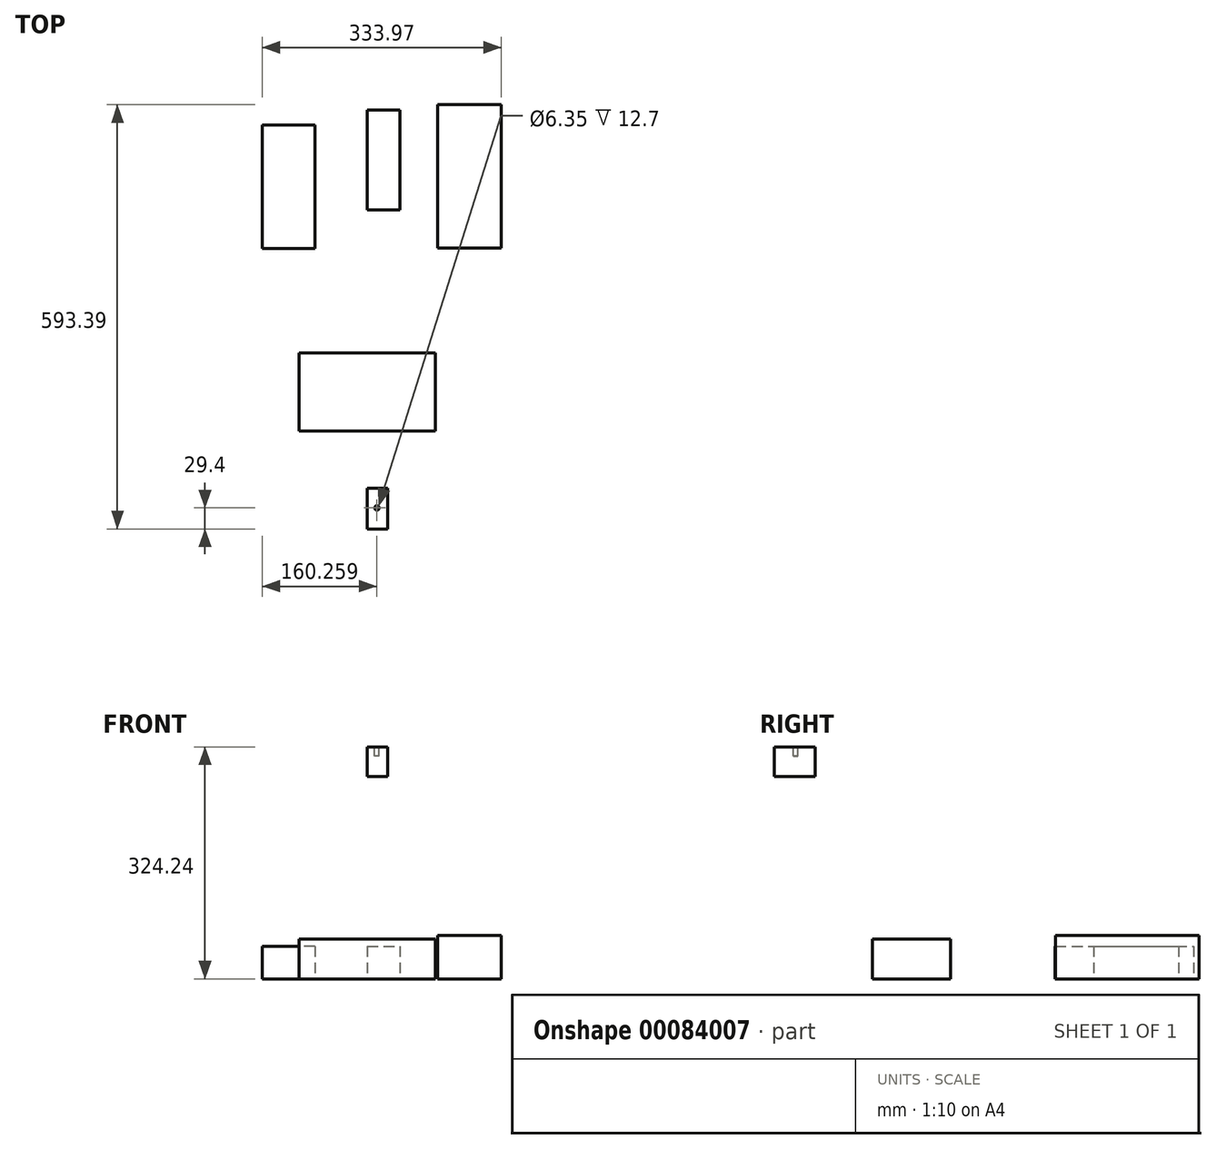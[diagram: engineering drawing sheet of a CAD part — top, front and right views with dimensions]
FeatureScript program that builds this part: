
annotation { "Feature Type Name" : "Feature", "Feature Type Description" : "" }
export const myFeature = defineFeature(function(context is Context, id is Id, definition is map)
    precondition{}
    {
        {
            var Q0;
            Q0=qCreatedBy(makeId("Top.planeOp"),FACE);
            var sketch = newSketch(context, id + "F0", { "sketchPlane" : qUnion([Q0])});
            skLineSegment(sketch, "E0.bottom", {"start": v(0, 0) * mm, "end": v(45.72, 0) * mm});
            skLineSegment(sketch, "E0.top", {"start": v(0, 139.7) * mm, "end": v(45.72, 139.7) * mm});
            skLineSegment(sketch, "E0.left", {"start": v(0, 0) * mm, "end": v(0, 139.7) * mm});
            skLineSegment(sketch, "E0.right", {"start": v(45.72, 0) * mm, "end": v(45.72, 139.7) * mm});
            skSolve(sketch);
        }
        {
            var Q0;
            Q0=makeQuery(id+"F0.imprint","IMPRINT",FACE,{"disambiguationData":[TD([[makeQuery(id+"F0.imprint","IMPRINT",EDGE,{"derivedFrom":sQuery(id+"F0.wireOp",EDGE,"E0.bottom")}),1.0]])]});
            extrude(context, id + "F1", {"entities" : qUnion([Q0]), "depth" : 45.72 * mm});
        }
        {
            var Q0;
            Q0=qCreatedBy(makeId("Top.planeOp"),FACE);
            var sketch = newSketch(context, id + "F2", { "sketchPlane" : qUnion([Q0])});
            skLineSegment(sketch, "E1.bottom", {"start": v(-72.96, -53.7) * mm, "end": v(-146.62, -53.7) * mm});
            skLineSegment(sketch, "E1.top", {"start": v(-72.96, 119.01) * mm, "end": v(-146.62, 119.01) * mm});
            skLineSegment(sketch, "E1.left", {"start": v(-72.96, -53.7) * mm, "end": v(-72.96, 119.01) * mm});
            skLineSegment(sketch, "E1.right", {"start": v(-146.62, -53.7) * mm, "end": v(-146.62, 119.01) * mm});
            skSolve(sketch);
        }
        {
            var Q0;
            Q0=makeQuery(id+"F2.imprint","IMPRINT",FACE,{"disambiguationData":[TD([[makeQuery(id+"F2.imprint","IMPRINT",EDGE,{"derivedFrom":sQuery(id+"F2.wireOp",EDGE,"E1.bottom")}),-1.0]])]});
            extrude(context, id + "F3", {"entities" : qUnion([Q0]), "depth" : 45.72 * mm});
        }
        {
            var Q0;
            Q0=qCreatedBy(makeId("Top.planeOp"),FACE);
            var sketch = newSketch(context, id + "F4", { "sketchPlane" : qUnion([Q0])});
            skLineSegment(sketch, "E2.bottom", {"start": v(98.45, -53.47) * mm, "end": v(187.35, -53.47) * mm});
            skLineSegment(sketch, "E2.top", {"start": v(98.45, 147.19) * mm, "end": v(187.35, 147.19) * mm});
            skLineSegment(sketch, "E2.left", {"start": v(98.45, -53.47) * mm, "end": v(98.45, 147.19) * mm});
            skLineSegment(sketch, "E2.right", {"start": v(187.35, -53.47) * mm, "end": v(187.35, 147.19) * mm});
            skSolve(sketch);
        }
        {
            var Q0;
            Q0=makeQuery(id+"F4.imprint","IMPRINT",FACE,{"disambiguationData":[TD([[makeQuery(id+"F4.imprint","IMPRINT",EDGE,{"derivedFrom":sQuery(id+"F4.wireOp",EDGE,"E2.bottom")}),1.0]])]});
            extrude(context, id + "F5", {"entities" : qUnion([Q0]), "depth" : 60.96 * mm});
        }
        {
            var Q0;
            Q0=qCreatedBy(makeId("Top.planeOp"),FACE);
            var sketch = newSketch(context, id + "F6", { "sketchPlane" : qUnion([Q0])});
            skLineSegment(sketch, "E3.bottom", {"start": v(-95.33, -199.86) * mm, "end": v(95.17, -199.86) * mm});
            skLineSegment(sketch, "E3.top", {"start": v(-95.33, -309.08) * mm, "end": v(95.17, -309.08) * mm});
            skLineSegment(sketch, "E3.left", {"start": v(-95.33, -199.86) * mm, "end": v(-95.33, -309.08) * mm});
            skLineSegment(sketch, "E3.right", {"start": v(95.17, -199.86) * mm, "end": v(95.17, -309.08) * mm});
            skSolve(sketch);
        }
        {
            var Q0;
            Q0=makeQuery(id+"F6.imprint","IMPRINT",FACE,{"disambiguationData":[TD([[makeQuery(id+"F6.imprint","IMPRINT",EDGE,{"derivedFrom":sQuery(id+"F6.wireOp",EDGE,"E3.bottom")}),-1.0]])]});
            extrude(context, id + "F7", {"entities" : qUnion([Q0]), "depth" : 55.88 * mm});
        }
        {
            var Q0;
            Q0=qCreatedBy(makeId("Right.planeOp"),FACE);
            var sketch = newSketch(context, id + "F8", { "sketchPlane" : qUnion([Q0])});
            skLineSegment(sketch, "E4.bottom", {"start": v(-446.2, 324.24) * mm, "end": v(-389.05, 324.24) * mm});
            skLineSegment(sketch, "E4.top", {"start": v(-446.2, 282.97) * mm, "end": v(-389.05, 282.97) * mm});
            skLineSegment(sketch, "E4.left", {"start": v(-446.2, 324.24) * mm, "end": v(-446.2, 282.97) * mm});
            skLineSegment(sketch, "E4.right", {"start": v(-389.05, 324.24) * mm, "end": v(-389.05, 282.97) * mm});
            skSolve(sketch);
        }
        {
            var Q0;
            Q0=makeQuery(id+"F8.imprint","IMPRINT",FACE,{"disambiguationData":[TD([[makeQuery(id+"F8.imprint","IMPRINT",EDGE,{"derivedFrom":sQuery(id+"F8.wireOp",EDGE,"E4.bottom")}),-1.0]])]});
            extrude(context, id + "F9", {"entities" : qUnion([Q0]), "depth" : 28.57 * mm});
        }
        {
            var Q0;
            Q0=makeQuery(id+"F9.opExtrude","SWEPT_FACE",FACE,{"disambiguationData":[OSD([sQuery(id+"F8.wireOp",EDGE,"E4.bottom")])]});
            var sketch = newSketch(context, id + "F10", { "sketchPlane" : qUnion([Q0])});
            skCircle(sketch, "E5", {"center": v(13.64, -416.8) * mm, "radius": 3.18 * mm});
            skSolve(sketch);
        }
        {
            var Q0;
            Q0=makeQuery(id+"F10.imprint","IMPRINT",FACE,{"disambiguationData":[TD([[makeQuery(id+"F10.imprint","IMPRINT",EDGE,{"derivedFrom":sQuery(id+"F10.wireOp",EDGE,"E5")}),1.0]])]});
            extrude(context, id + "F11", {"entities" : qUnion([Q0]), "operationType" : NewBodyOperationType.REMOVE, "oppositeDirection" : true, "depth" : 12.7 * mm});
        }
    });
